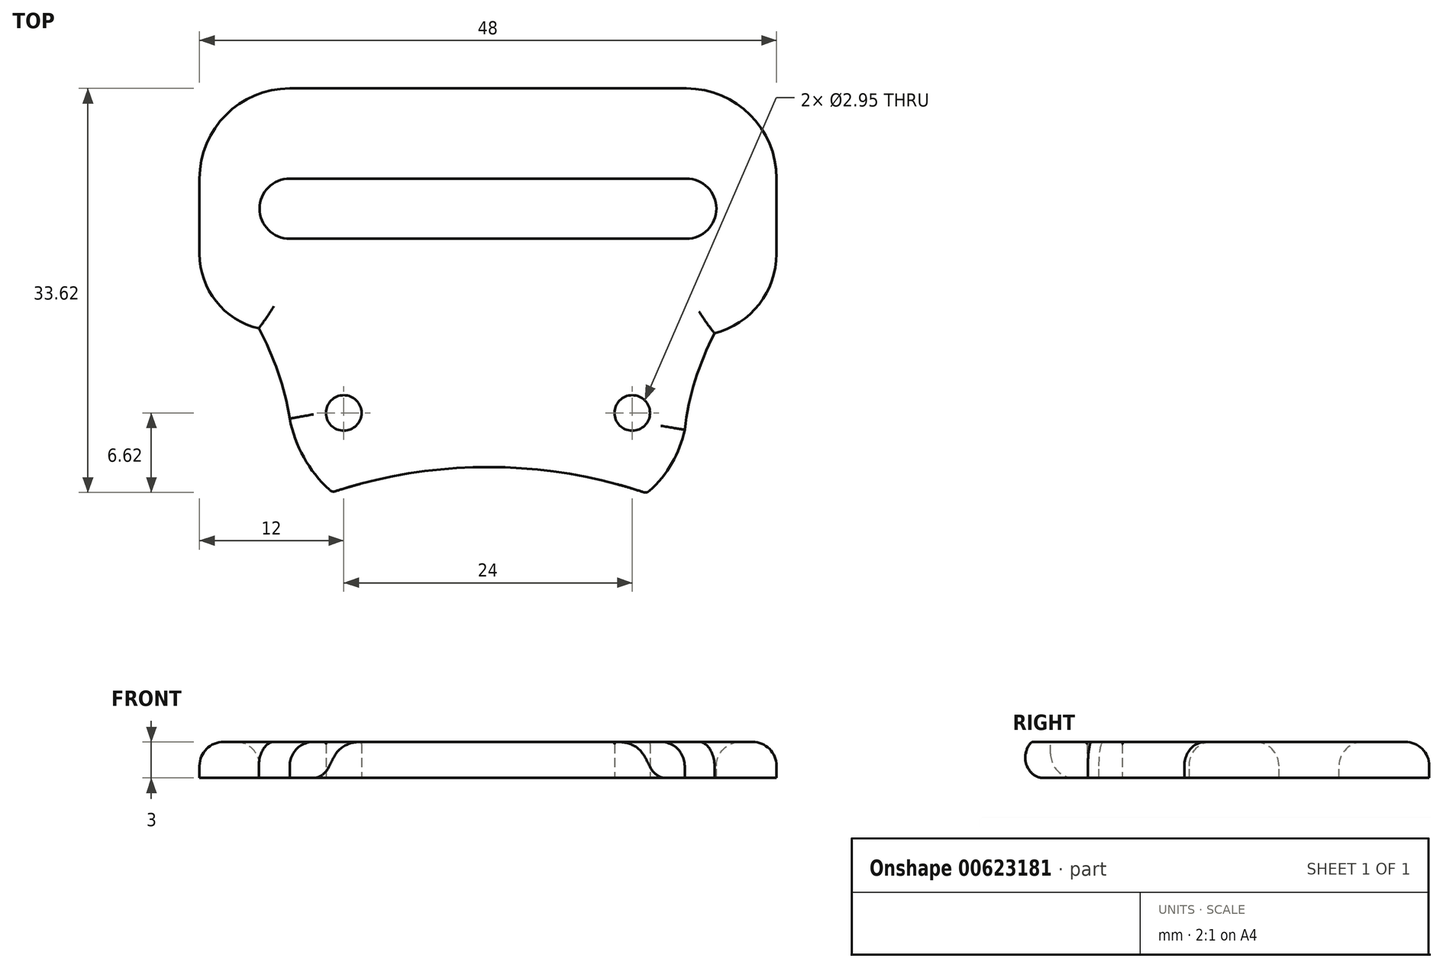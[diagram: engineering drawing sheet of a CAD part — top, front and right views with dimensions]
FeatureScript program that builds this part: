
annotation { "Feature Type Name" : "Feature", "Feature Type Description" : "" }
export const myFeature = defineFeature(function(context is Context, id is Id, definition is map)
    precondition{}
    {
        {
            var Q0;
            Q0=qCreatedBy(makeId("Top.planeOp"),FACE);
            var sketch = newSketch(context, id + "F0", { "sketchPlane" : qUnion([Q0])});
            skLineSegment(sketch, "E0.bottom", {"start": v(16.5, 2.5) * mm, "end": v(-16.5, 2.5) * mm});
            skLineSegment(sketch, "E0.top", {"start": v(16.5, -2.5) * mm, "end": v(-16.5, -2.5) * mm});
            skLineSegment(sketch, "E0.left", {"start": v(19, 0) * mm, "end": v(19, 0) * mm});
            skLineSegment(sketch, "E0.right", {"start": v(-19, 0) * mm, "end": v(-19, 0) * mm});
            skPoint(sketch, "E0.middle", {"position": v(0, 0) * mm});
            skPoint(sketch, "E1.visualSharp", {"position": v(-19, 2.5) * mm});
            skArc(sketch, "E1.filletArc", {"start": v(-16.5, 2.5) * mm, "mid": v(-18.27, 1.77) * mm, "end": v(-19, 0) * mm});
            skPoint(sketch, "E2.visualSharp", {"position": v(-19, -2.5) * mm});
            skArc(sketch, "E2.filletArc", {"start": v(-19, 0) * mm, "mid": v(-18.27, -1.77) * mm, "end": v(-16.5, -2.5) * mm});
            skPoint(sketch, "E3.visualSharp", {"position": v(19, -2.5) * mm});
            skArc(sketch, "E3.filletArc", {"start": v(16.5, -2.5) * mm, "mid": v(18.27, -1.77) * mm, "end": v(19, 0) * mm});
            skPoint(sketch, "E4.visualSharp", {"position": v(19, 2.5) * mm});
            skArc(sketch, "E4.filletArc", {"start": v(19, 0) * mm, "mid": v(18.27, 1.77) * mm, "end": v(16.5, 2.5) * mm});
            skLineSegment(sketch, "E5.bottom", {"start": v(16.5, -10) * mm, "end": v(-16.5, -10) * mm});
            skLineSegment(sketch, "E5.left", {"start": v(24, -2.5) * mm, "end": v(24, 3.75) * mm});
            skLineSegment(sketch, "E5.right", {"start": v(-24, -2.5) * mm, "end": v(-24, 3.75) * mm});
            skPoint(sketch, "E6.visualSharp", {"position": v(-24, -10) * mm});
            skArc(sketch, "E6.filletArc", {"start": v(-24, -2.5) * mm, "mid": v(-21.8, -7.8) * mm, "end": v(-16.5, -10) * mm});
            skPoint(sketch, "E7.visualSharp", {"position": v(24, -10) * mm});
            skArc(sketch, "E7.filletArc", {"start": v(16.5, -10) * mm, "mid": v(21.8, -7.8) * mm, "end": v(24, -2.5) * mm});
            skArc(sketch, "E8", {"start": v(-12.96, 23.6) * mm, "mid": v(0.12, 21.5) * mm, "end": v(13.2, 23.68) * mm});
            skLineSegment(sketch, "E9", {"start": v(0, 21.5) * mm, "end": v(0, 0) * mm, "construction": true});
            skArc(sketch, "E10", {"start": v(16.36, 18.4) * mm, "mid": v(17.24, 14.28) * mm, "end": v(18.84, 10.38) * mm});
            skArc(sketch, "E11", {"start": v(-19.07, 9.97) * mm, "mid": v(-17.47, 13.6) * mm, "end": v(-16.5, 17.47) * mm});
            skArc(sketch, "E12", {"start": v(16.5, 17.47) * mm, "mid": v(15.46, 20.9) * mm, "end": v(13.2, 23.68) * mm});
            skArc(sketch, "E13", {"start": v(-12.96, 23.6) * mm, "mid": v(-15.25, 20.83) * mm, "end": v(-16.5, 17.47) * mm});
            skArc(sketch, "E14", {"start": v(24, 3.75) * mm, "mid": v(22.56, 7.95) * mm, "end": v(18.84, 10.38) * mm});
            skArc(sketch, "E15", {"start": v(-19.07, 9.97) * mm, "mid": v(-22.62, 7.72) * mm, "end": v(-24, 3.75) * mm});
            skSolve(sketch);
        }
        {
            var Q0;
            Q0 = qSketchRegion(id + "F0", true);
            extrude(context, id + "F1", {"entities" : qUnion([Q0]), "depth" : 3 * mm, "offsetDistance" : 25 * mm});
        }
        {
            var Q0;
            Q0=makeQuery(id+"F1.opExtrude","CAP_FACE",FACE,{"disambiguationData":[OSD([sQuery(id+"F0.wireOp",EDGE,"E0.bottom"),sQuery(id+"F0.wireOp",EDGE,"E0.top"),sQuery(id+"F0.wireOp",EDGE,"E1.filletArc"),sQuery(id+"F0.wireOp",EDGE,"E2.filletArc"),sQuery(id+"F0.wireOp",EDGE,"E3.filletArc"),sQuery(id+"F0.wireOp",EDGE,"E4.filletArc"),sQuery(id+"F0.wireOp",EDGE,"E5.bottom"),sQuery(id+"F0.wireOp",EDGE,"E5.left"),sQuery(id+"F0.wireOp",EDGE,"E5.right"),sQuery(id+"F0.wireOp",EDGE,"E6.filletArc"),sQuery(id+"F0.wireOp",EDGE,"E7.filletArc"),sQuery(id+"F0.wireOp",EDGE,"E8"),sQuery(id+"F0.wireOp",EDGE,"E10"),sQuery(id+"F0.wireOp",EDGE,"E11"),sQuery(id+"F0.wireOp",EDGE,"E12"),sQuery(id+"F0.wireOp",EDGE,"E13"),sQuery(id+"F0.wireOp",EDGE,"E14"),sQuery(id+"F0.wireOp",EDGE,"E15")])],"isStart":false});
            var sketch = newSketch(context, id + "F2", { "sketchPlane" : qUnion([Q0])});
            skLineSegment(sketch, "E16", {"start": v(0, 0) * mm, "end": v(0, 17) * mm, "construction": true});
            skLineSegment(sketch, "E17", {"start": v(0, 17) * mm, "end": v(-12, 17) * mm, "construction": true});
            skLineSegment(sketch, "E18", {"start": v(0, 17) * mm, "end": v(12, 17) * mm, "construction": true});
            skCircle(sketch, "E19", {"center": v(-12, 17) * mm, "radius": 1.48 * mm});
            skCircle(sketch, "E20", {"center": v(12, 17) * mm, "radius": 1.48 * mm});
            skSolve(sketch);
        }
        {
            var Q0;
            Q0 = qSketchRegion(id + "F2", true);
            extrude(context, id + "F3", {"entities" : qUnion([Q0]), "operationType" : NewBodyOperationType.REMOVE, "oppositeDirection" : true, "depth" : 5 * mm, "offsetDistance" : 25 * mm});
        }
        {
            var Q0;
            Q0=makeQuery(id+"F1.opExtrude","CAP_EDGE",EDGE,{"disambiguationData":[OSD([sQuery(id+"F0.wireOp",EDGE,"E5.left")])],"isStart":true});
            var Q1;
            Q1=makeQuery(id+"F1.opExtrude","CAP_EDGE",EDGE,{"disambiguationData":[OSD([sQuery(id+"F0.wireOp",EDGE,"E7.filletArc")])],"isStart":true});
            var Q2;
            Q2=makeQuery(id+"F1.opExtrude","CAP_EDGE",EDGE,{"disambiguationData":[OSD([sQuery(id+"F0.wireOp",EDGE,"E5.bottom")])],"isStart":true});
            var Q3;
            Q3=makeQuery(id+"F1.opExtrude","CAP_EDGE",EDGE,{"disambiguationData":[OSD([sQuery(id+"F0.wireOp",EDGE,"E6.filletArc")])],"isStart":true});
            var Q4;
            Q4=makeQuery(id+"F1.opExtrude","CAP_EDGE",EDGE,{"disambiguationData":[OSD([sQuery(id+"F0.wireOp",EDGE,"E5.right")])],"isStart":true});
            var Q5;
            Q5=makeQuery(id+"F1.opExtrude","CAP_EDGE",EDGE,{"disambiguationData":[OSD([sQuery(id+"F0.wireOp",EDGE,"E15")])],"isStart":true});
            var Q6;
            Q6=makeQuery(id+"F1.opExtrude","CAP_EDGE",EDGE,{"disambiguationData":[OSD([sQuery(id+"F0.wireOp",EDGE,"E11")])],"isStart":true});
            var Q7;
            Q7=makeQuery(id+"F1.opExtrude","CAP_EDGE",EDGE,{"disambiguationData":[OSD([sQuery(id+"F0.wireOp",EDGE,"E13")])],"isStart":true});
            var Q8;
            Q8=makeQuery(id+"F1.opExtrude","CAP_EDGE",EDGE,{"disambiguationData":[OSD([sQuery(id+"F0.wireOp",EDGE,"E12")])],"isStart":true});
            var Q9;
            Q9=makeQuery(id+"F1.opExtrude","CAP_EDGE",EDGE,{"disambiguationData":[OSD([sQuery(id+"F0.wireOp",EDGE,"E10")])],"isStart":true});
            var Q10;
            Q10=makeQuery(id+"F1.opExtrude","CAP_EDGE",EDGE,{"disambiguationData":[OSD([sQuery(id+"F0.wireOp",EDGE,"E14")])],"isStart":true});
            var Q11;
            Q11=makeQuery(id+"F1.opExtrude","CAP_EDGE",EDGE,{"disambiguationData":[OSD([sQuery(id+"F0.wireOp",EDGE,"E0.bottom")])],"isStart":true});
            fillet(context, id + "F4", {"entities" : qUnion([Q0, Q1, Q2, Q3, Q4, Q5, Q6, Q7, Q8, Q9, Q10, Q11]), "radius" : 2 * mm, "tangentPropagation" : true, "allowEdgeOverflow" : false});
        }
        {
            var Q0;
            Q0=makeQuery(id+"F1.opExtrude","CAP_EDGE",EDGE,{"disambiguationData":[OSD([sQuery(id+"F0.wireOp",EDGE,"E8")])],"isStart":false});
            fillet(context, id + "F5", {"entities" : qUnion([Q0]), "radius" : 2 * mm, "tangentPropagation" : true, "allowEdgeOverflow" : false});
        }
        {
            var Q0;
            Q0=makeQuery(id+"F3.boolean.opBoolean","COPY",EDGE,{"derivedFrom":makeQuery(id+"F3.opExtrude","CAP_EDGE",EDGE,{"disambiguationData":[OSD([sQuery(id+"F2.wireOp",EDGE,"E19")])],"isStart":true})});
            var Q1;
            Q1=makeQuery(id+"F3.boolean.opBoolean","COPY",EDGE,{"derivedFrom":makeQuery(id+"F3.opExtrude","CAP_EDGE",EDGE,{"disambiguationData":[OSD([sQuery(id+"F2.wireOp",EDGE,"E20")])],"isStart":true})});
            var Q2;
            Q2=makeQuery(id+"F3.boolean.opBoolean","INTERSECT",EDGE,{"derivedFrom":[makeQuery(id+"F1.opExtrude","CAP_FACE",FACE,{"disambiguationData":[OSD([sQuery(id+"F0.wireOp",EDGE,"E0.bottom"),sQuery(id+"F0.wireOp",EDGE,"E0.top"),sQuery(id+"F0.wireOp",EDGE,"E1.filletArc"),sQuery(id+"F0.wireOp",EDGE,"E2.filletArc"),sQuery(id+"F0.wireOp",EDGE,"E3.filletArc"),sQuery(id+"F0.wireOp",EDGE,"E4.filletArc"),sQuery(id+"F0.wireOp",EDGE,"E5.bottom"),sQuery(id+"F0.wireOp",EDGE,"E5.left"),sQuery(id+"F0.wireOp",EDGE,"E5.right"),sQuery(id+"F0.wireOp",EDGE,"E6.filletArc"),sQuery(id+"F0.wireOp",EDGE,"E7.filletArc"),sQuery(id+"F0.wireOp",EDGE,"E8"),sQuery(id+"F0.wireOp",EDGE,"E10"),sQuery(id+"F0.wireOp",EDGE,"E11"),sQuery(id+"F0.wireOp",EDGE,"E12"),sQuery(id+"F0.wireOp",EDGE,"E13"),sQuery(id+"F0.wireOp",EDGE,"E14"),sQuery(id+"F0.wireOp",EDGE,"E15")])],"isStart":true}),makeQuery(id+"F3.opExtrude","SWEPT_FACE",FACE,{"disambiguationData":[OSD([sQuery(id+"F2.wireOp",EDGE,"E19")])]})]});
            var Q3;
            Q3=makeQuery(id+"F3.boolean.opBoolean","INTERSECT",EDGE,{"derivedFrom":[makeQuery(id+"F1.opExtrude","CAP_FACE",FACE,{"disambiguationData":[OSD([sQuery(id+"F0.wireOp",EDGE,"E0.bottom"),sQuery(id+"F0.wireOp",EDGE,"E0.top"),sQuery(id+"F0.wireOp",EDGE,"E1.filletArc"),sQuery(id+"F0.wireOp",EDGE,"E2.filletArc"),sQuery(id+"F0.wireOp",EDGE,"E3.filletArc"),sQuery(id+"F0.wireOp",EDGE,"E4.filletArc"),sQuery(id+"F0.wireOp",EDGE,"E5.bottom"),sQuery(id+"F0.wireOp",EDGE,"E5.left"),sQuery(id+"F0.wireOp",EDGE,"E5.right"),sQuery(id+"F0.wireOp",EDGE,"E6.filletArc"),sQuery(id+"F0.wireOp",EDGE,"E7.filletArc"),sQuery(id+"F0.wireOp",EDGE,"E8"),sQuery(id+"F0.wireOp",EDGE,"E10"),sQuery(id+"F0.wireOp",EDGE,"E11"),sQuery(id+"F0.wireOp",EDGE,"E12"),sQuery(id+"F0.wireOp",EDGE,"E13"),sQuery(id+"F0.wireOp",EDGE,"E14"),sQuery(id+"F0.wireOp",EDGE,"E15")])],"isStart":true}),makeQuery(id+"F3.opExtrude","SWEPT_FACE",FACE,{"disambiguationData":[OSD([sQuery(id+"F2.wireOp",EDGE,"E20")])]})]});
            fillet(context, id + "F6", {"entities" : qUnion([Q0, Q1, Q2, Q3]), "radius" : .2 * mm, "tangentPropagation" : true, "allowEdgeOverflow" : false});
        }
        {
            var Q0;
            Q0=makeQuery(id+"F1.opExtrude","SWEPT_BODY",BODY,{"disambiguationData":[OSD([sQuery(id+"F0.wireOp",EDGE,"E0.bottom"),sQuery(id+"F0.wireOp",EDGE,"E0.top"),sQuery(id+"F0.wireOp",EDGE,"E1.filletArc"),sQuery(id+"F0.wireOp",EDGE,"E2.filletArc"),sQuery(id+"F0.wireOp",EDGE,"E3.filletArc"),sQuery(id+"F0.wireOp",EDGE,"E4.filletArc"),sQuery(id+"F0.wireOp",EDGE,"E5.bottom"),sQuery(id+"F0.wireOp",EDGE,"E5.left"),sQuery(id+"F0.wireOp",EDGE,"E5.right"),sQuery(id+"F0.wireOp",EDGE,"E6.filletArc"),sQuery(id+"F0.wireOp",EDGE,"E7.filletArc"),sQuery(id+"F0.wireOp",EDGE,"E8"),sQuery(id+"F0.wireOp",EDGE,"E10"),sQuery(id+"F0.wireOp",EDGE,"E11"),sQuery(id+"F0.wireOp",EDGE,"E12"),sQuery(id+"F0.wireOp",EDGE,"E13"),sQuery(id+"F0.wireOp",EDGE,"E14"),sQuery(id+"F0.wireOp",EDGE,"E15")])]});
            var Q1;
            Q1=makeQuery(id+"F1.opExtrude","CAP_EDGE",EDGE,{"disambiguationData":[OSD([sQuery(id+"F0.wireOp",EDGE,"E0.bottom")])],"isStart":false});
            transform(context, id + "F7", {"entities" : qUnion([Q0]), "transformType" : TransformType.ROTATION, "transformAxis" : qUnion([Q1]), "angle" : 180 * degree, "makeCopy" : false});
        }
    });
